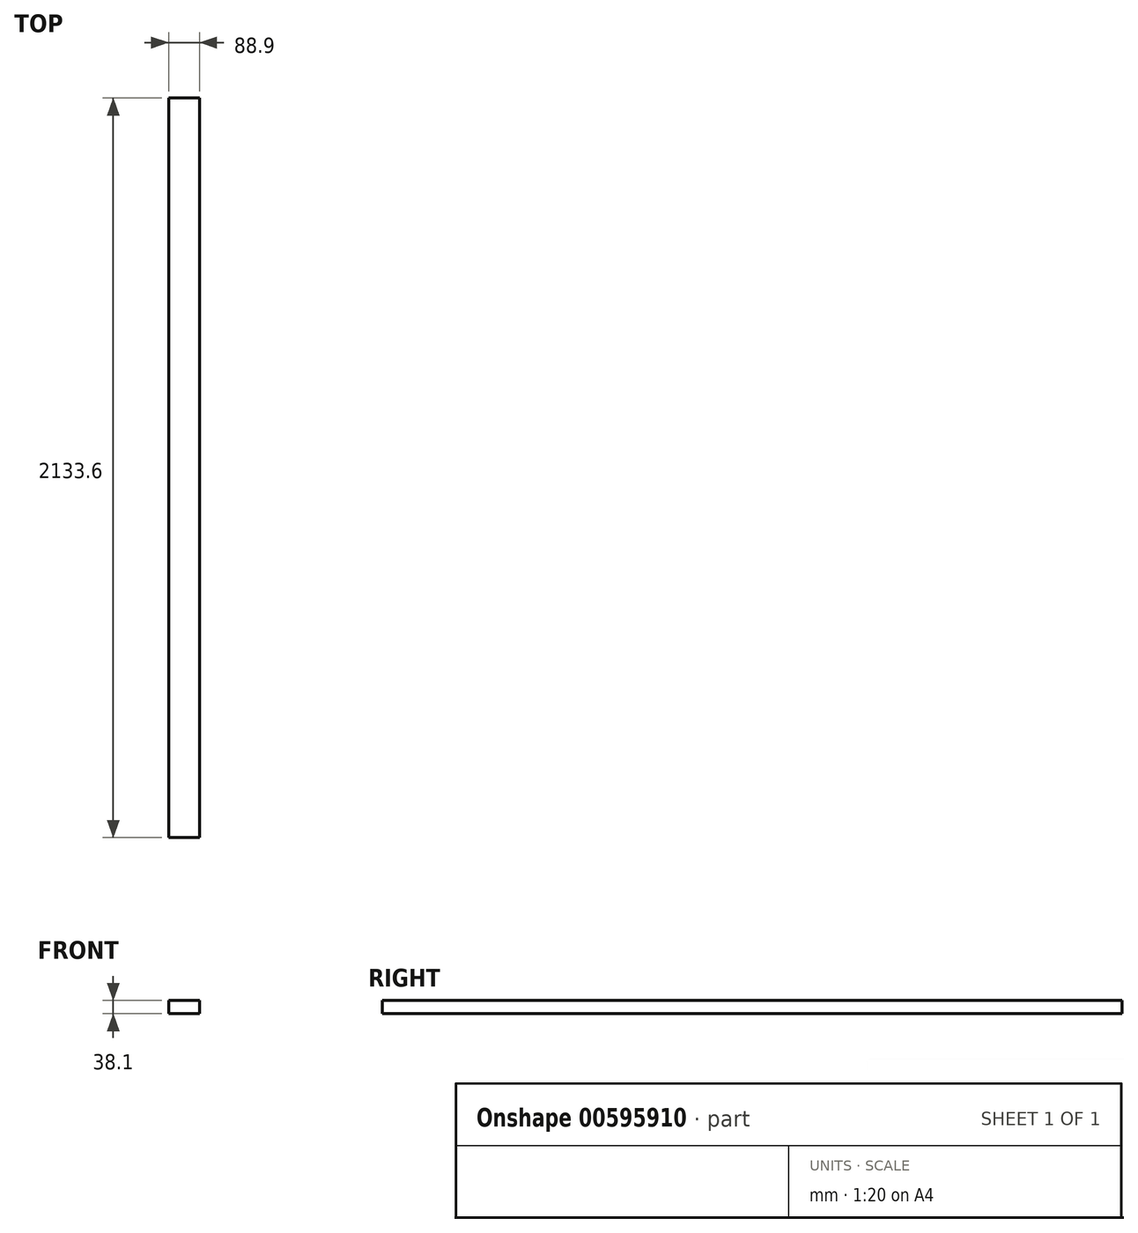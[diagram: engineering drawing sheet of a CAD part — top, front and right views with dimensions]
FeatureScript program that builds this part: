
annotation { "Feature Type Name" : "Feature", "Feature Type Description" : "" }
export const myFeature = defineFeature(function(context is Context, id is Id, definition is map)
    precondition{}
    {
        {
            var Q0;
            Q0=qCreatedBy(makeId("Front.planeOp"),FACE);
            var sketch = newSketch(context, id + "F0", { "sketchPlane" : qUnion([Q0])});
            skLineSegment(sketch, "E0.bottom", {"start": v(0, 0) * mm, "end": v(88.9, 0) * mm});
            skLineSegment(sketch, "E0.top", {"start": v(0, 38.1) * mm, "end": v(88.9, 38.1) * mm});
            skLineSegment(sketch, "E0.left", {"start": v(0, 0) * mm, "end": v(0, 38.1) * mm});
            skLineSegment(sketch, "E0.right", {"start": v(88.9, 0) * mm, "end": v(88.9, 38.1) * mm});
            skSolve(sketch);
        }
        {
            var Q0;
            Q0=makeQuery(id+"F0.imprint","IMPRINT",FACE,{"disambiguationData":[TD([[makeQuery(id+"F0.imprint","IMPRINT",EDGE,{"derivedFrom":sQuery(id+"F0.wireOp",EDGE,"E0.bottom")}),1.0]])]});
            extrude(context, id + "F1", {"entities" : qUnion([Q0]), "depth" : 2133.6 * mm, "offsetDistance" : 25.4 * mm});
        }
    });
